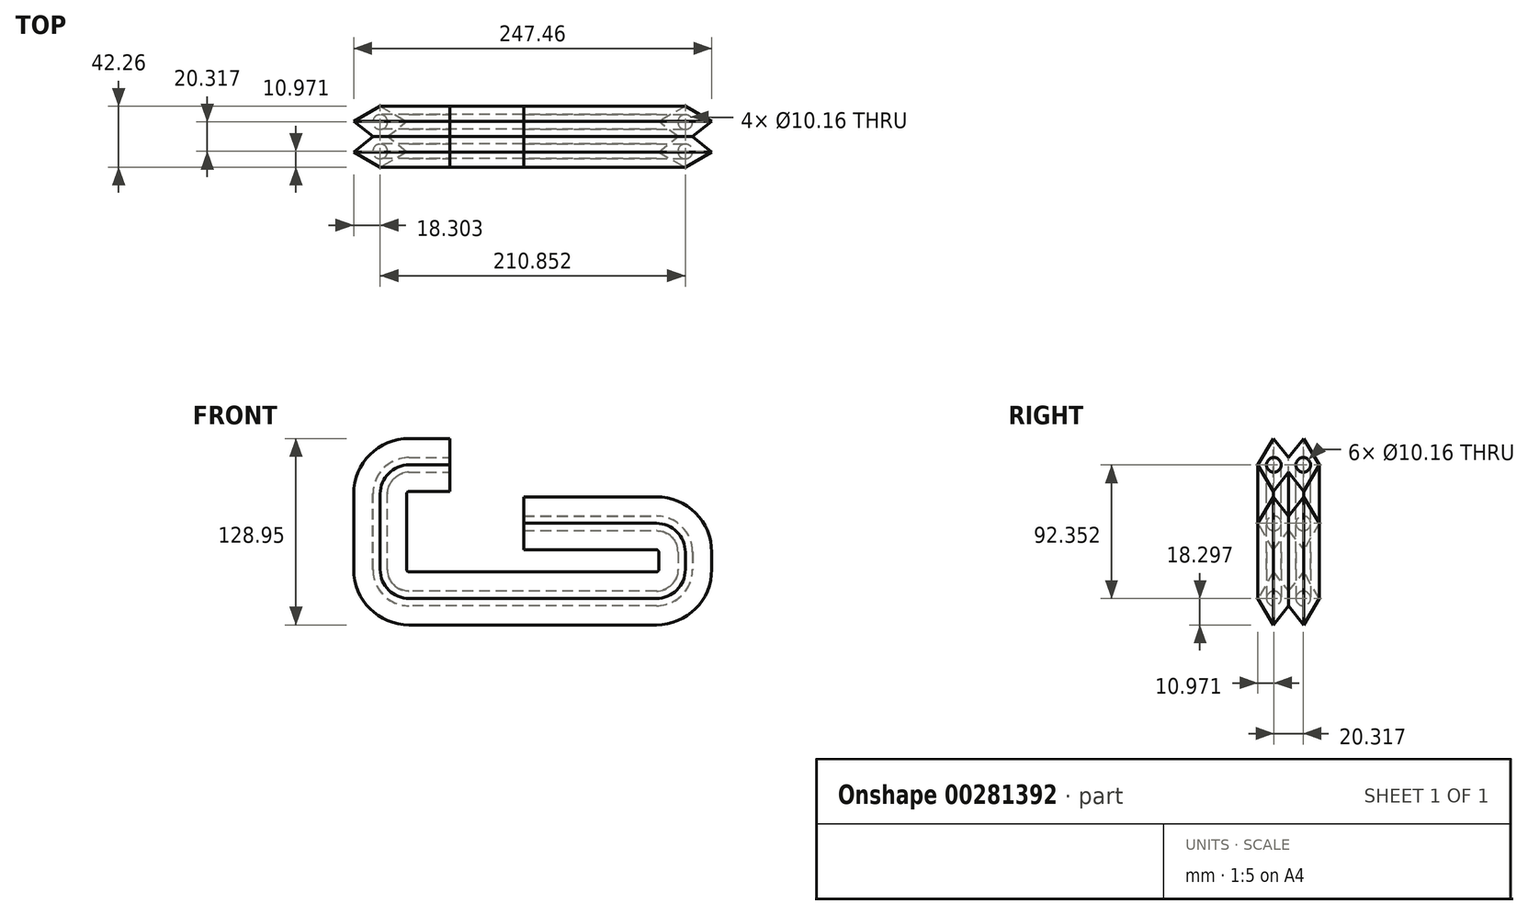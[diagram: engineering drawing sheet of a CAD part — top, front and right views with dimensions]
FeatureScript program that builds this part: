
annotation { "Feature Type Name" : "Feature", "Feature Type Description" : "" }
export const myFeature = defineFeature(function(context is Context, id is Id, definition is map)
    precondition{}
    {
        {
            var Q0;
            Q0=qCreatedBy(makeId("Right.planeOp"),FACE);
            var sketch = newSketch(context, id + "F0", { "sketchPlane" : qUnion([Q0])});
            skArc(sketch, "E0.cCircle", {"start": v(-8.78, 16.06) * mm, "mid": v(-18.3, 0) * mm, "end": v(-8.78, -16.06) * mm, "construction": true});
            skLineSegment(sketch, "E0.1", {"start": v(10.57, 18.3) * mm, "end": v(21.13, 0) * mm});
            skLineSegment(sketch, "E0.2", {"start": v(21.13, 0) * mm, "end": v(10.57, -18.3) * mm});
            skLineSegment(sketch, "E0.4", {"start": v(-10.57, -18.3) * mm, "end": v(-21.13, 0) * mm});
            skLineSegment(sketch, "E0.5", {"start": v(-21.13, 0) * mm, "end": v(-10.57, 18.3) * mm});
            skPoint(sketch, "E0.0.midPoint", {"position": v(0, 18.3) * mm});
            skLineSegment(sketch, "E1", {"start": v(0, -5) * mm, "end": v(10.57, -18.3) * mm});
            skLineSegment(sketch, "E2", {"start": v(-10.57, 18.3) * mm, "end": v(0, 5) * mm});
            skLineSegment(sketch, "E3", {"start": v(0, 5) * mm, "end": v(10.57, 18.3) * mm});
            skLineSegment(sketch, "E4", {"start": v(-10.57, -18.3) * mm, "end": v(0, -5) * mm});
            skArc(sketch, "E5.trimOffspring", {"start": v(8.78, -16.06) * mm, "mid": v(18.3, 0) * mm, "end": v(8.78, 16.06) * mm, "construction": true});
            skCircle(sketch, "E6", {"center": v(-10.16, 0) * mm, "radius": 5.08 * mm});
            skCircle(sketch, "E7.MirrorC", {"center": v(10.16, 0) * mm, "radius": 5.08 * mm});
            skSolve(sketch);
        }
        {
            var Q0;
            Q0=qCreatedBy(makeId("Front.planeOp"),FACE);
            var sketch = newSketch(context, id + "F1", { "sketchPlane" : qUnion([Q0])});
            skLineSegment(sketch, "E8", {"start": v(0, 0) * mm, "end": v(91.64, 0) * mm});
            skLineSegment(sketch, "E9", {"start": v(111.64, -20) * mm, "end": v(111.64, -31.95) * mm});
            skLineSegment(sketch, "E10", {"start": v(91.64, -51.95) * mm, "end": v(-79.22, -51.95) * mm});
            skLineSegment(sketch, "E11", {"start": v(-99.22, -31.95) * mm, "end": v(-99.22, 20.4) * mm});
            skLineSegment(sketch, "E12", {"start": v(-79.22, 40.4) * mm, "end": v(-51.03, 40.4) * mm});
            skPoint(sketch, "E13.visualSharp", {"position": v(0, 0) * mm});
            skPoint(sketch, "E14.visualSharp", {"position": v(111.64, 0) * mm});
            skArc(sketch, "E15.filletArc", {"start": v(111.64, -20) * mm, "mid": v(105.78, -5.86) * mm, "end": v(91.64, 0) * mm});
            skPoint(sketch, "E16.visualSharp", {"position": v(111.64, -51.95) * mm});
            skArc(sketch, "E16.filletArc", {"start": v(91.64, -51.95) * mm, "mid": v(105.78, -46.1) * mm, "end": v(111.64, -31.95) * mm});
            skPoint(sketch, "E17.visualSharp", {"position": v(-99.22, -51.95) * mm});
            skArc(sketch, "E17.filletArc", {"start": v(-99.22, -31.95) * mm, "mid": v(-93.36, -46.1) * mm, "end": v(-79.22, -51.95) * mm});
            skPoint(sketch, "E18.visualSharp", {"position": v(-99.22, 40.4) * mm});
            skArc(sketch, "E18.filletArc", {"start": v(-79.22, 40.4) * mm, "mid": v(-93.36, 34.54) * mm, "end": v(-99.22, 20.4) * mm});
            skSolve(sketch);
        }
        {
            var Q0;
            Q0=makeQuery(id+"F0.imprint","IMPRINT",FACE,{"disambiguationData":[TD([[makeQuery(id+"F0.imprint","IMPRINT",EDGE,{"derivedFrom":sQuery(id+"F0.wireOp",EDGE,"E0.1")}),-1.0]])]});
            var Q1;
            Q1=sQuery(id+"F1.wireOp",EDGE,"E8");
            var Q2;
            Q2=sQuery(id+"F1.wireOp",EDGE,"E15.filletArc");
            var Q3;
            Q3=sQuery(id+"F1.wireOp",EDGE,"E9");
            var Q4;
            Q4=sQuery(id+"F1.wireOp",EDGE,"E16.filletArc");
            var Q5;
            Q5=sQuery(id+"F1.wireOp",EDGE,"E10");
            var Q6;
            Q6=sQuery(id+"F1.wireOp",EDGE,"E17.filletArc");
            var Q7;
            Q7=sQuery(id+"F1.wireOp",EDGE,"E11");
            var Q8;
            Q8=sQuery(id+"F1.wireOp",EDGE,"E18.filletArc");
            var Q9;
            Q9=sQuery(id+"F1.wireOp",EDGE,"E12");
            sweep(context, id + "F2", {"profiles" : qUnion([Q0]), "path" : qUnion([Q1, Q2, Q3, Q4, Q5, Q6, Q7, Q8, Q9])});
        }
    });
